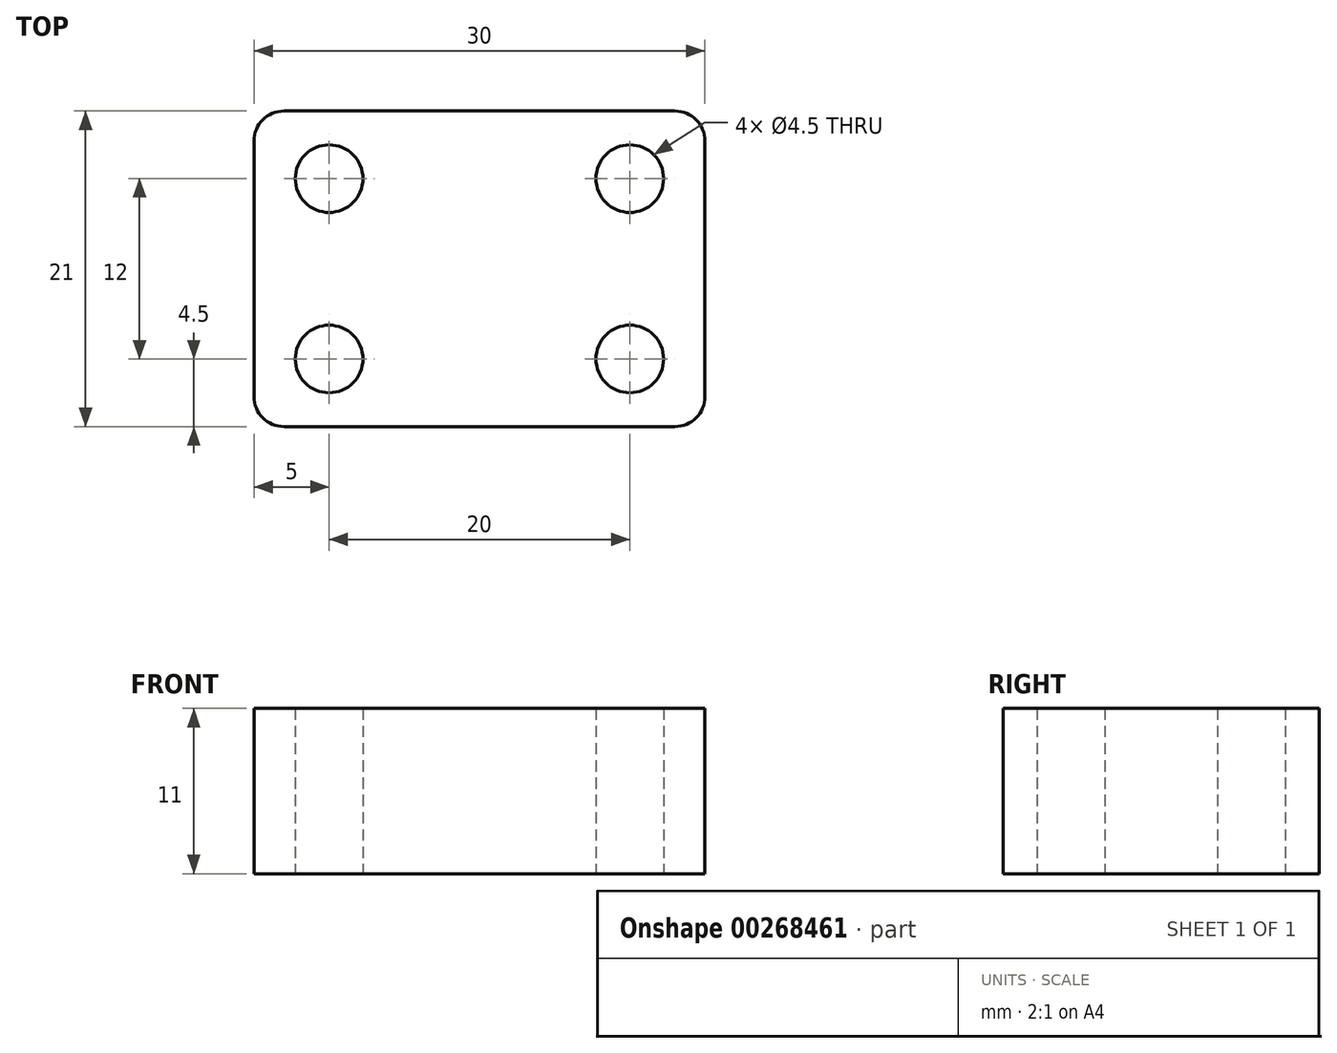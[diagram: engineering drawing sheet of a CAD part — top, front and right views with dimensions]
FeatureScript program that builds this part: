
annotation { "Feature Type Name" : "Feature", "Feature Type Description" : "" }
export const myFeature = defineFeature(function(context is Context, id is Id, definition is map)
    precondition{}
    {
        {
            var Q0;
            Q0=qCreatedBy(makeId("Top.planeOp"),FACE);
            var sketch = newSketch(context, id + "F0", { "sketchPlane" : qUnion([Q0])});
            skLineSegment(sketch, "E0.bottom", {"start": v(0, 0) * mm, "end": v(30, 0) * mm});
            skLineSegment(sketch, "E0.top", {"start": v(0, 21) * mm, "end": v(30, 21) * mm});
            skLineSegment(sketch, "E0.left", {"start": v(0, 0) * mm, "end": v(0, 21) * mm});
            skLineSegment(sketch, "E0.right", {"start": v(30, 0) * mm, "end": v(30, 21) * mm});
            skCircle(sketch, "E1", {"center": v(5, 16.5) * mm, "radius": 2.25 * mm});
            skCircle(sketch, "E2", {"center": v(25, 16.5) * mm, "radius": 2.25 * mm});
            skCircle(sketch, "E3", {"center": v(5, 4.5) * mm, "radius": 2.25 * mm});
            skCircle(sketch, "E4", {"center": v(25, 4.5) * mm, "radius": 2.25 * mm});
            skSolve(sketch);
        }
        {
            var Q0;
            Q0=makeQuery(id+"F0.imprint","IMPRINT",FACE,{"disambiguationData":[TD([[makeQuery(id+"F0.imprint","IMPRINT",EDGE,{"derivedFrom":sQuery(id+"F0.wireOp",EDGE,"E0.bottom")}),1.0]])]});
            extrude(context, id + "F1", {"entities" : qUnion([Q0]), "depth" : 11 * mm});
        }
        {
            var Q0;
            Q0=makeQuery(id+"F1.opExtrude","SWEPT_EDGE",EDGE,{"disambiguationData":[OSD([sQuery(id+"F0.wireOp",EDGE,"E0.bottom"),sQuery(id+"F0.wireOp",EDGE,"E0.right")])]});
            var Q1;
            Q1=makeQuery(id+"F1.opExtrude","SWEPT_EDGE",EDGE,{"disambiguationData":[OSD([sQuery(id+"F0.wireOp",EDGE,"E0.top"),sQuery(id+"F0.wireOp",EDGE,"E0.right")])]});
            var Q2;
            Q2=makeQuery(id+"F1.opExtrude","SWEPT_EDGE",EDGE,{"disambiguationData":[OSD([sQuery(id+"F0.wireOp",EDGE,"E0.top"),sQuery(id+"F0.wireOp",EDGE,"E0.left")])]});
            var Q3;
            Q3=makeQuery(id+"F1.opExtrude","SWEPT_EDGE",EDGE,{"disambiguationData":[OSD([sQuery(id+"F0.wireOp",EDGE,"E0.bottom"),sQuery(id+"F0.wireOp",EDGE,"E0.left")])]});
            fillet(context, id + "F2", {"entities" : qUnion([Q0, Q1, Q2, Q3]), "radius" : 2 * mm, "tangentPropagation" : true, "allowEdgeOverflow" : false});
        }
    });
